# Revit family: Sanitary_Wash-Basins_DURAVIT-AG_D-Neo-Washbasin-White-High-Gloss-550-mm-236655
name_source: partatom
category: Plumbing Fixtures
revit_build: Autodesk Revit 2018 (Build: 20190510_1515(x64)
units: mm (PartAtom-declared; Revit-internal decimal feet)

## family parameters
Cut with Voids When Loaded = No
Host = Face
OmniClass Number = 23.21.43.23
OmniClass Title = Sanitary Waste Receptacles
Part Type = Normal
Room Calculation Point = No
Round Connector Dimension = Use Diameter
Shared = No

## types (1)
- D-Neo Washbasin White High Gloss 550 mm - 236655
    Always visible = Yes
    BIMobject category = Wash Basins
    Date of publishing = 05.05.2021 00:00:00
    Default Elevation = 1219.2 mm  [stored 4 ft]
    Description = D-Neo offers perfectly thought-through design and the highest quality at an attractive price and matches any decorating style. The visual highlight of the ceramic is the striking, all around rim. The washbasin, also glazed underneath, with overflow as well as with faucet hole platform is available in three different sizes (55, 60 or 65 cm).
    Diameter = 31.75 mm
    Edition number = 1
    IFC Classification = Sanitary Terminal
    Installation instructions = https://duravit-public-assets.s3.eu-central-1.amazonaws.com
    Main material = Duravit - Ceramic - 00 - White Alpin
    Manufacturer = Duravit
    Manufacturer name = DURAVIT AG
    Masterformat 2014 Code = 22 45 26
    Masterformat 2014 Description = Eye/Face Wash Equipment
    Material main = Ceramics
    Model = D-Neo Washbasin White High Gloss 550 mm - 236655
    NBS Reference Code = 31-76
    NBS Reference Description = Sanitary Dispensing And Disposal Units
    OmniClass Code = 23-21 43 23
    OmniClass Description = Sanitary Waste Receptacles
    Product Guid = 01afeb3f-6cd3-40e8-95c4-66149d22f407
    Product SKU = d-neo-sink-236655
    Product data url = https://bimobject.com
    Product family = D-Neo
    Product group = Sink
    Product name = D-Neo Washbasin White High Gloss 550 mm - 236655
    QR code = https://bimobject.com
    UNSPSC Code = 301815
    URL = https://www.duravit.com
    Uniclass 1.4 Code = L721
    Uniclass 1.4 Description = Sanitary equipment
    Uniclass 2.0 Code = PR-31-76
    Uniclass 2.0 Description = Sanitary Dispensing And Disposal Units
    Uniclass 2015 Code = Pr_40_20_96
    Uniclass 2015 Name = Wash basins, sinks and troughs
    Uniformat II Code = E1010
    Uniformat II Description = Commercial Equipment
    Weight Net (Kg) = 15,8

note: [stored X ft] marks values corroborated as IEEE doubles in the binary element streams (Revit-internal decimal feet)

## geometry (parser evidence)
native form markers: Sweep x4
no freeform markers — native parametric forms only
